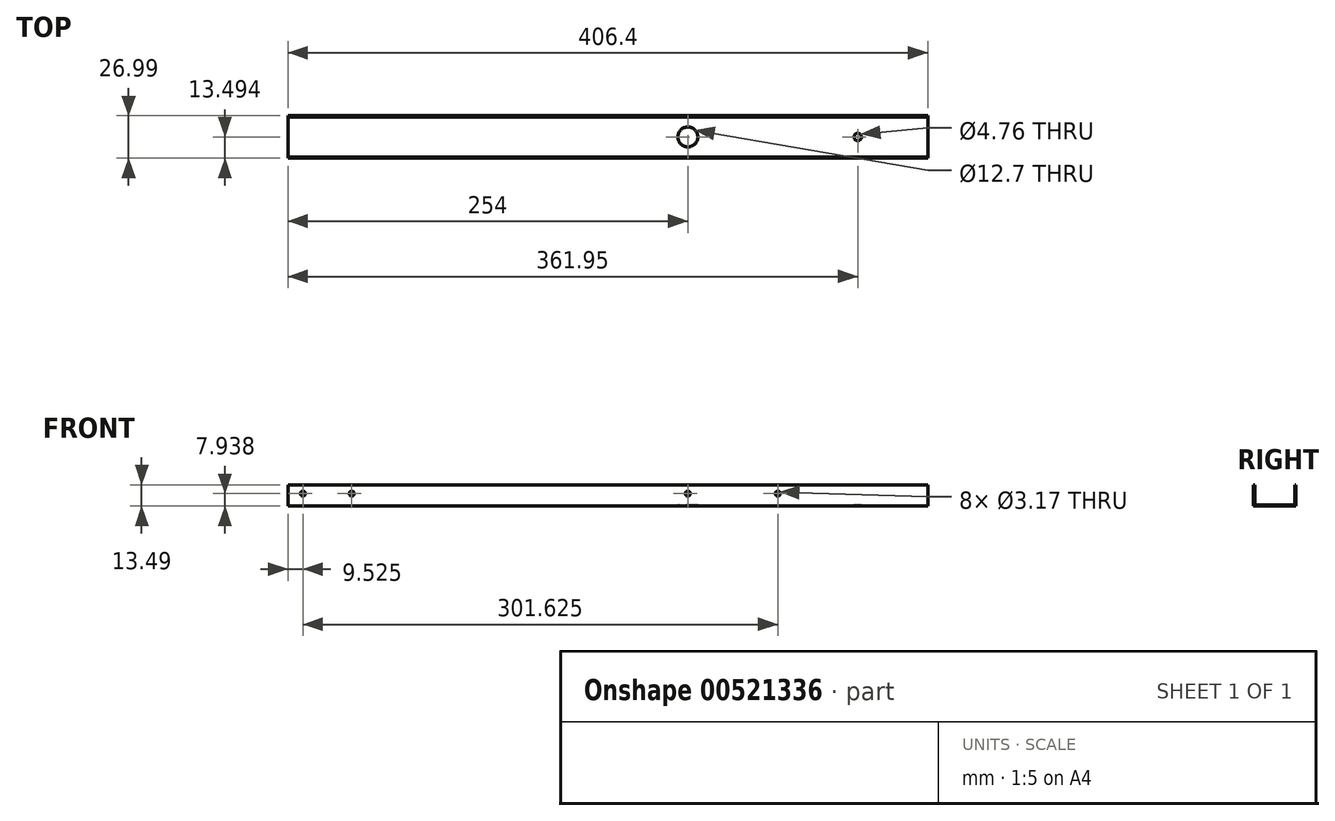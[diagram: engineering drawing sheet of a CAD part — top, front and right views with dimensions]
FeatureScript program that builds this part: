
annotation { "Feature Type Name" : "Feature", "Feature Type Description" : "" }
export const myFeature = defineFeature(function(context is Context, id is Id, definition is map)
    precondition{}
    {
        {
            var Q0;
            Q0=qCreatedBy(makeId("Top.planeOp"),FACE);
            var sketch = newSketch(context, id + "F0", { "sketchPlane" : qUnion([Q0])});
            skLineSegment(sketch, "E0.bottom", {"start": v(0, 0) * mm, "end": v(406.4, 0) * mm});
            skLineSegment(sketch, "E0.top", {"start": v(0, 26.99) * mm, "end": v(406.4, 26.99) * mm});
            skLineSegment(sketch, "E0.left", {"start": v(0, 0) * mm, "end": v(0, 26.99) * mm});
            skLineSegment(sketch, "E0.right", {"start": v(406.4, 0) * mm, "end": v(406.4, 26.99) * mm});
            skSolve(sketch);
        }
        {
            var Q0;
            Q0 = qSketchRegion(id + "F0", true);
            extrude(context, id + "F1", {"entities" : qUnion([Q0]), "depth" : 0.8 * mm, "offsetDistance" : 25.4 * mm});
        }
        {
            var Q0;
            Q0=makeQuery(id+"F1.opExtrude","CAP_FACE",FACE,{"disambiguationData":[OSD([sQuery(id+"F0.wireOp",EDGE,"E0.bottom"),sQuery(id+"F0.wireOp",EDGE,"E0.top"),sQuery(id+"F0.wireOp",EDGE,"E0.left"),sQuery(id+"F0.wireOp",EDGE,"E0.right")])],"isStart":false});
            var sketch = newSketch(context, id + "F2", { "sketchPlane" : qUnion([Q0])});
            skLineSegment(sketch, "E1", {"start": v(0, 13.5) * mm, "end": v(406.4, 13.5) * mm, "construction": true});
            skLineSegment(sketch, "E2.0.0", {"start": v(406.4, 26.99) * mm, "end": v(0, 26.99) * mm});
            skLineSegment(sketch, "E2.0.1", {"start": v(0, 26.99) * mm, "end": v(0, 0) * mm});
            skLineSegment(sketch, "E2.0.2", {"start": v(0, 0) * mm, "end": v(406.4, 0) * mm});
            skLineSegment(sketch, "E2.0.3", {"start": v(406.4, 0) * mm, "end": v(406.4, 26.99) * mm});
            skLineSegment(sketch, "E3", {"start": v(0, 26.2) * mm, "end": v(406.4, 26.2) * mm});
            skLineSegment(sketch, "E4.MirrorCS", {"start": v(0, 0.8) * mm, "end": v(406.4, 0.8) * mm});
            skSolve(sketch);
        }
        {
            var Q0;
            {var subQ0=sQuery(id+"F2.wireOp",EDGE,"E2.0.0");Q0=makeQuery(id+"F2.imprint","IMPRINT",FACE,{"disambiguationData":[TD([[makeQuery(id+"F2.imprint","IMPRINT",EDGE,{"derivedFrom":subQ0}),-1.0]])]});}
            var Q1;
            {var subQ0=sQuery(id+"F2.wireOp",EDGE,"E2.0.2");Q1=makeQuery(id+"F2.imprint","IMPRINT",FACE,{"disambiguationData":[TD([[makeQuery(id+"F2.imprint","IMPRINT",EDGE,{"derivedFrom":subQ0}),1.0]])]});}
            extrude(context, id + "F3", {"entities" : qUnion([Q0, Q1]), "operationType" : NewBodyOperationType.ADD, "depth" : 12.7 * mm, "offsetDistance" : 25.4 * mm});
        }
        {
            var Q0;
            Q0=makeQuery(id+"F3.boolean.opBoolean","MERGE",FACE,{"derivedFrom":[makeQuery(id+"F1.opExtrude","SWEPT_FACE",FACE,{"disambiguationData":[OSD([sQuery(id+"F0.wireOp",EDGE,"E0.bottom")])]}),makeQuery(id+"F3.opExtrude","SWEPT_FACE",FACE,{"disambiguationData":[OSD([sQuery(id+"F2.wireOp",EDGE,"E2.0.2")])]})]});
            var sketch = newSketch(context, id + "F4", { "sketchPlane" : qUnion([Q0])});
            skCircle(sketch, "E5", {"center": v(311.15, 7.94) * mm, "radius": 1.59 * mm});
            skCircle(sketch, "E6", {"center": v(254, 7.94) * mm, "radius": 1.59 * mm});
            skCircle(sketch, "E7", {"center": v(40.48, 7.94) * mm, "radius": 1.59 * mm});
            skCircle(sketch, "E8", {"center": v(9.53, 7.94) * mm, "radius": 1.59 * mm});
            skSolve(sketch);
        }
        {
            var Q0;
            Q0 = qSketchRegion(id + "F4", true);
            extrude(context, id + "F5", {"entities" : qUnion([Q0]), "operationType" : NewBodyOperationType.REMOVE, "endBound" : BoundingType.THROUGH_ALL, "oppositeDirection" : true, "depth" : 25.4 * mm, "offsetDistance" : 25.4 * mm});
        }
        {
            var Q0;
            Q0=makeQuery(id+"F1.opExtrude","CAP_FACE",FACE,{"disambiguationData":[OSD([sQuery(id+"F0.wireOp",EDGE,"E0.bottom"),sQuery(id+"F0.wireOp",EDGE,"E0.top"),sQuery(id+"F0.wireOp",EDGE,"E0.left"),sQuery(id+"F0.wireOp",EDGE,"E0.right")])],"isStart":false});
            var sketch = newSketch(context, id + "F6", { "sketchPlane" : qUnion([Q0])});
            skLineSegment(sketch, "E9.0", {"start": v(252.41, 26.2) * mm, "end": v(255.59, 26.2) * mm});
            skCircle(sketch, "E10", {"center": v(254, 13.5) * mm, "radius": 6.35 * mm});
            skPoint(sketch, "E10.centerSnap0", {"position": v(406.4, 13.5) * mm});
            skPoint(sketch, "E10.centerSnap1", {"position": v(254, 26.2) * mm});
            skCircle(sketch, "E11", {"center": v(361.95, 13.5) * mm, "radius": 2.38 * mm});
            skSolve(sketch);
        }
        {
            var Q0;
            Q0 = qSketchRegion(id + "F6", true);
            extrude(context, id + "F7", {"entities" : qUnion([Q0]), "operationType" : NewBodyOperationType.REMOVE, "oppositeDirection" : true, "depth" : 25.4 * mm, "offsetDistance" : 25.4 * mm});
        }
    });
